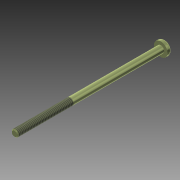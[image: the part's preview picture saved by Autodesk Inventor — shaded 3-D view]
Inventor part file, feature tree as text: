
AUTODESK INVENTOR PART (.ipt)
format: ipt  version: 2018 (Build 220112000, 112)  size: 115,712 bytes
history: native  units: mm
features: imported_body x1, thread x1
ambient origin geometry x8: Origin, YZ Plane, XZ Plane, XY Plane, X Axis, Y Axis, Z Axis, Center Point
bodies: Solid1 (feature_tree)
feature tree (2):
  imported_body  "Base1"
  thread  "Thread1"  [1 undecoded]
note: 1 required parameter value undecoded (feature->parameter linkage not recoverable at this tier; creation-order binding heuristic only, values carry confidence <= 0.55)
